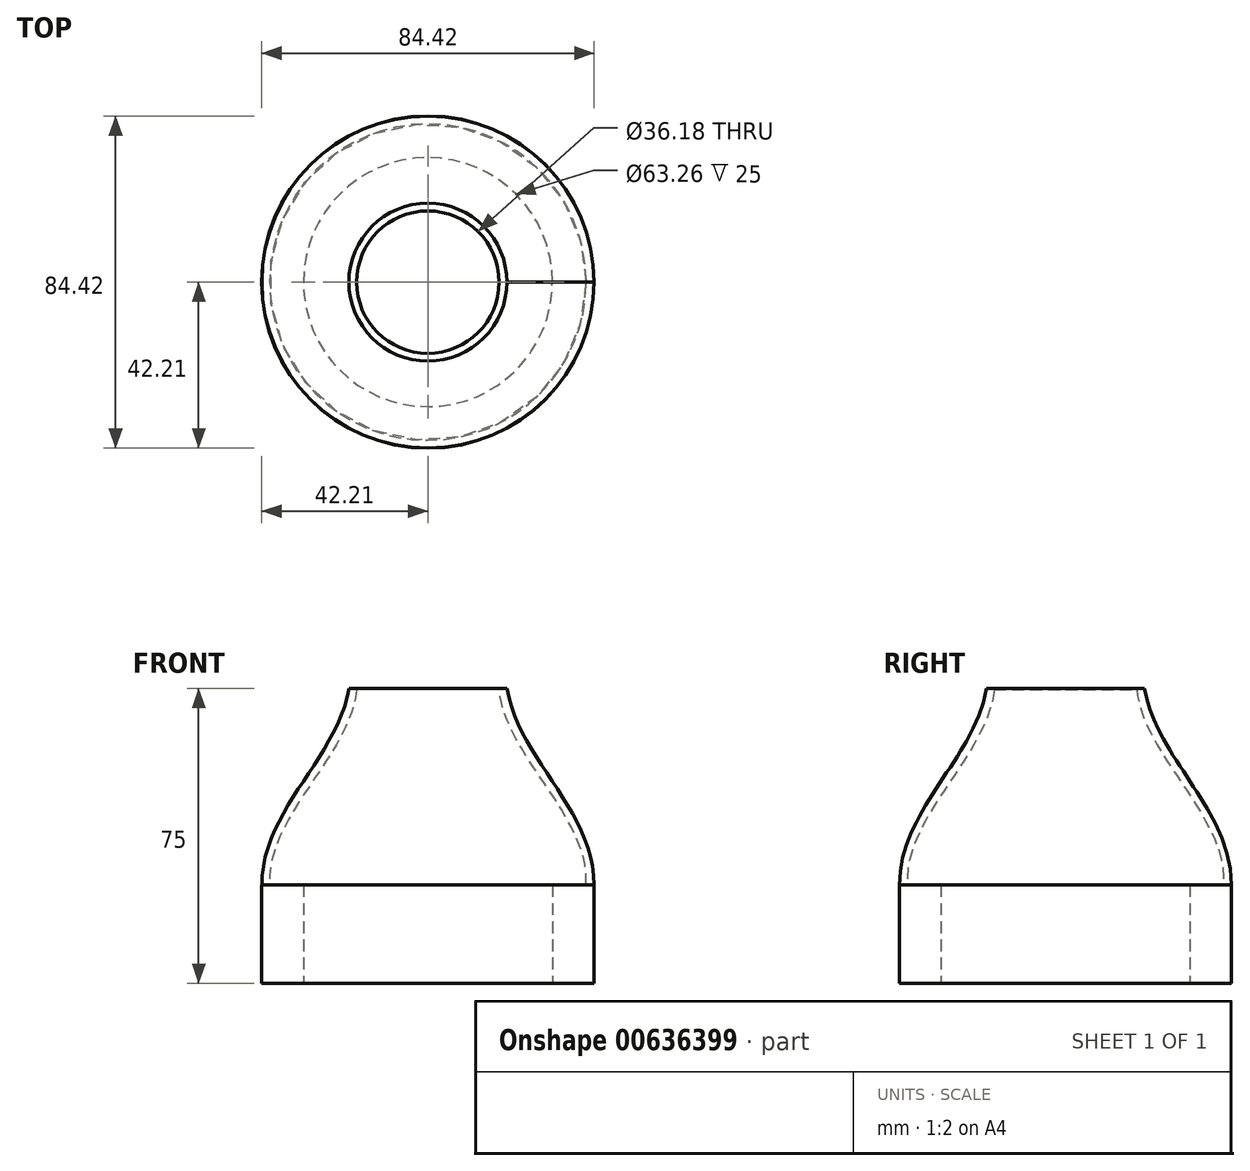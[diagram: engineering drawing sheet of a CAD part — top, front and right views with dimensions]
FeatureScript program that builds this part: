
annotation { "Feature Type Name" : "Feature", "Feature Type Description" : "" }
export const myFeature = defineFeature(function(context is Context, id is Id, definition is map)
    precondition{}
    {
        {
            var Q0;
            Q0=qCreatedBy(makeId("Top.planeOp"),FACE);
            var sketch = newSketch(context, id + "F0", { "sketchPlane" : qUnion([Q0])});
            skCircle(sketch, "E0", {"center": v(0, 0) * mm, "radius": 42.2 * mm});
            skCircle(sketch, "E1", {"center": v(0, 0) * mm, "radius": 31.63 * mm});
            skSolve(sketch);
        }
        {
            var Q0;
            Q0=makeQuery(id+"F0.imprint","IMPRINT",FACE,{"disambiguationData":[TD([[makeQuery(id+"F0.imprint","IMPRINT",EDGE,{"derivedFrom":sQuery(id+"F0.wireOp",EDGE,"E0")}),1.0]])]});
            extrude(context, id + "F1", {"entities" : qUnion([Q0]), "depth" : 25 * mm, "offsetDistance" : 25 * mm});
        }
        {
            var Q0;
            Q0=makeQuery(id+"F1.opExtrude","CAP_FACE",FACE,{"disambiguationData":[OSD([sQuery(id+"F0.wireOp",EDGE,"E0"),sQuery(id+"F0.wireOp",EDGE,"E1")])],"isStart":false});
            cPlane(context, id + "F2", {"entities" : qUnion([Q0]), "cplaneType" : CPlaneType.OFFSET, "offset" : 50 * mm, "width" : 150 * mm, "height" : 150 * mm});
        }
        {
            var Q0;
            Q0=qCreatedBy(makeId("Front.planeOp"),FACE);
            var sketch = newSketch(context, id + "F3", { "sketchPlane" : qUnion([Q0])});
            skFitSpline(sketch, "E2", {"points": [v(-42.17, 25) * mm, v(-20.06, 75) * mm], "startDerivative": vector(0, 57.64) * mm, "endDerivative": vector(9.2, 54.27) * mm});
            skFitSpline(sketch, "E3.0", {"points": [v(-40.17, 25) * mm, v(-40.17, 27.24) * mm, v(-39.62, 31.52) * mm, v(-37.48, 37.6) * mm, v(-34.36, 43.5) * mm, v(-30.63, 49.32) * mm, v(-26.7, 55.18) * mm, v(-22.95, 61.23) * mm, v(-19.85, 67.64) * mm, v(-18.5, 72.25) * mm, v(-18.1, 74.66) * mm]});
            skLineSegment(sketch, "E4", {"start": v(-40.17, 25.23) * mm, "end": v(-40.17, 25) * mm});
            skLineSegment(sketch, "E5", {"start": v(-40.17, 25) * mm, "end": v(-42.17, 25) * mm});
            skLineSegment(sketch, "E6", {"start": v(-18.1, 74.66) * mm, "end": v(-18.1, 75) * mm});
            skLineSegment(sketch, "E7", {"start": v(-18.1, 75) * mm, "end": v(-20.06, 75) * mm});
            skLineSegment(sketch, "E8", {"start": v(0, 75.1) * mm, "end": v(0, 0) * mm});
            skSolve(sketch);
        }
        {
            var Q0;
            Q0=makeQuery(id+"F3.imprint","IMPRINT",FACE,{"disambiguationData":[TD([[makeQuery(id+"F3.imprint","IMPRINT",EDGE,{"derivedFrom":sQuery(id+"F3.wireOp",EDGE,"E2")}),-1.0]])]});
            var Q1;
            Q1=sQuery(id+"F3.wireOp",EDGE,"E8");
            revolve(context, id + "F4", {"entities" : qUnion([Q0]), "axis" : qUnion([Q1]), "revolveType" : RevolveType.FULL});
        }
    });
